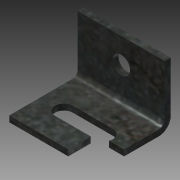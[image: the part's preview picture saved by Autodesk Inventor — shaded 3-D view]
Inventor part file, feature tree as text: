
AUTODESK INVENTOR PART (.ipt)
format: ipt  version: 2015 (Build 190159000, 159)  size: 200,192 bytes
history: native  units: in
note: dims shown in document units (in); Inventor stores cm internally (conversion verified against a paired STEP export)
features: sketch x8, sheet_metal_op x4, other x4, projected_geometry x4, hole x1
ambient origin geometry x8: Origin, YZ Plane, XZ Plane, XY Plane, X Axis, Y Axis, Z Axis, Center Point
bodies: Solid1 (feature_tree)
feature tree (21):
  sheet_metal_op  "Face1"
  sheet_metal_op  "Flange1"
  sketch  "Sketch3"  dims[d3=0.06in]
  hole  "Hole1"  [1 undecoded]
  sketch  "Sketch7"  dims[d5=0.12in]
  sketch  "Sketch8"  dims[d6=0.06in]
  sketch  "Sketch9"  dims[d7=0.625in d8=90.0deg d9=0.06in]
  sketch  "Sketch1"  dims[d0=0.875in d1=0.75in]
  other  "Plate1"
  sketch  "Sketch2"  dims[d2=0.06in]
  other  "Plate2"
  sheet_metal_op  "Bend1"
  sheet_metal_op  "Corner1"
  projected_geometry  "Projected Loop1"
  sketch  "Sketch4"  dims[d4=0.03in]
  projected_geometry  "Projected Loop2"
  projected_geometry  "Projected Loop3"
  projected_geometry  "Projected Loop4"
  sketch  "Sketch10"  dims[d10=0.24in d11=0.06in d12=0.06in d13=0.63in d14=0.875in d15=0.875in d16=0.505in d17=0.177in d18=0.75in d19=0.332in d20=0.25in d21=0.5635in d22=0.06in d23=0.8108in d24=0.177in d25=0.146in d26=0.06in d27=0.0in d28=0.625in d29=0.505in d30=0.875in d31=0.75in d32=0.63in d34=0.203in d35=0.281in d36=0.281in d37=0.281in d38=0.06in d39=0.0in]
  other  "Cut1"
  other  "Cut2"
note: 1 required parameter value undecoded (feature->parameter linkage not recoverable at this tier; creation-order binding heuristic only, values carry confidence <= 0.55)
